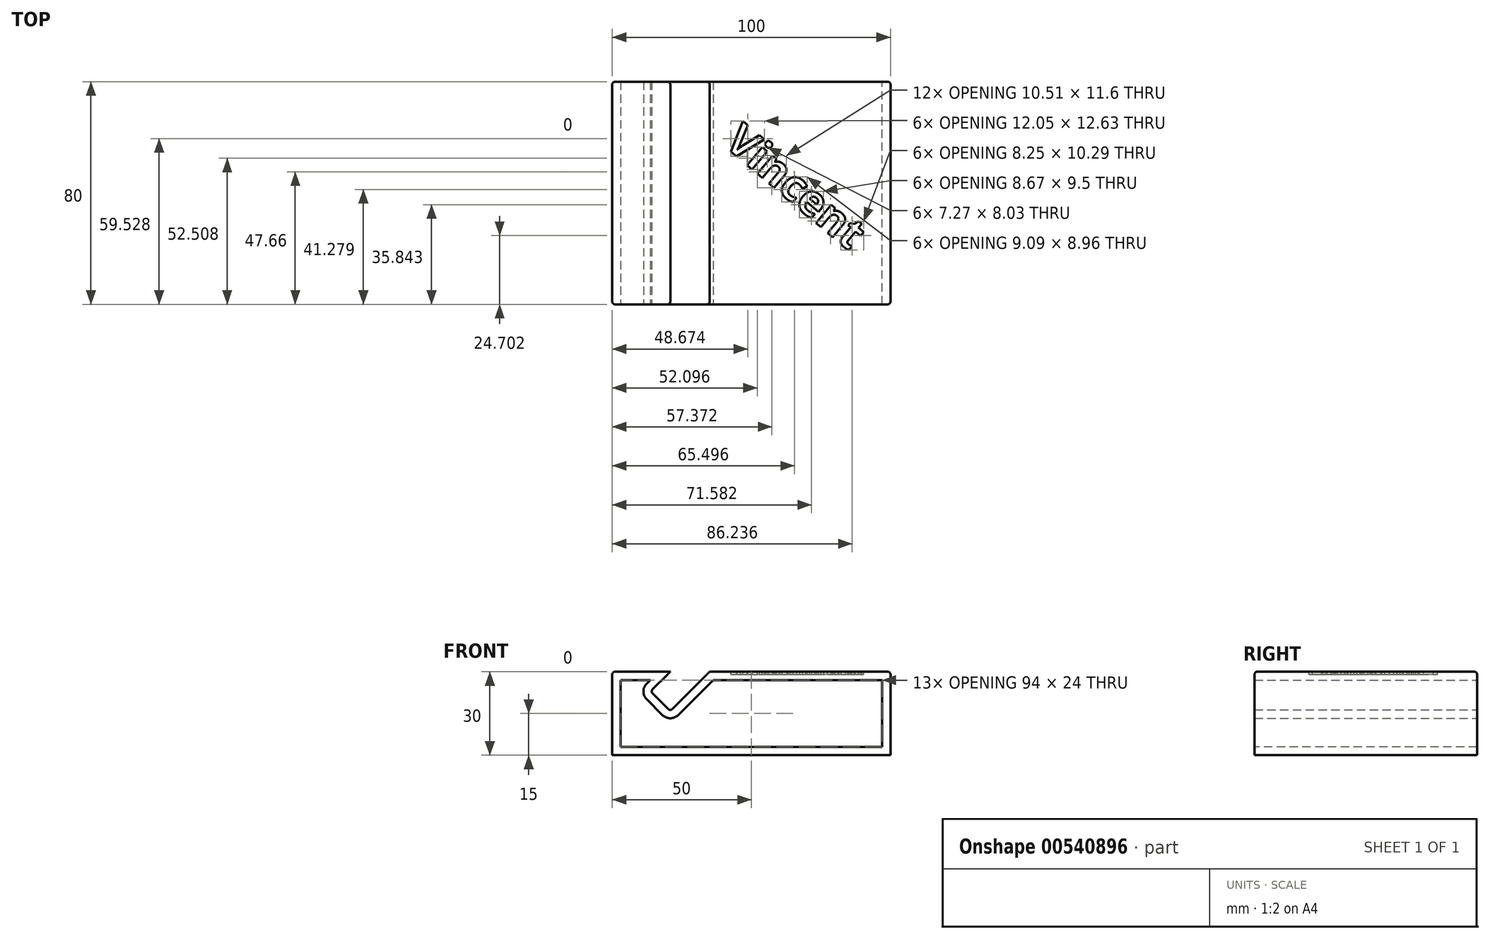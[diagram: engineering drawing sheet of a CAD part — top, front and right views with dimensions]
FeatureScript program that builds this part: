
annotation { "Feature Type Name" : "Feature", "Feature Type Description" : "" }
export const myFeature = defineFeature(function(context is Context, id is Id, definition is map)
    precondition{}
    {
        {
            var Q0;
            Q0=qCreatedBy(makeId("Top.planeOp"),FACE);
            var sketch = newSketch(context, id + "F0", { "sketchPlane" : qUnion([Q0])});
            skLineSegment(sketch, "E0.bottom", {"start": v(-45.15, 40.95) * mm, "end": v(54.85, 40.95) * mm});
            skLineSegment(sketch, "E0.top", {"start": v(-45.15, -39.05) * mm, "end": v(54.85, -39.05) * mm});
            skLineSegment(sketch, "E0.left", {"start": v(-45.15, 40.95) * mm, "end": v(-45.15, -39.05) * mm});
            skLineSegment(sketch, "E0.right", {"start": v(54.85, 40.95) * mm, "end": v(54.85, -39.05) * mm});
            skSolve(sketch);
        }
        {
            var Q0;
            Q0=makeQuery(id+"F0.imprint","IMPRINT",FACE,{"disambiguationData":[TD([[makeQuery(id+"F0.imprint","IMPRINT",EDGE,{"derivedFrom":sQuery(id+"F0.wireOp",EDGE,"E0.bottom")}),-1.0]])]});
            extrude(context, id + "F1", {"entities" : qUnion([Q0]), "depth" : 30 * mm, "offsetDistance" : 25 * mm});
        }
        {
            var Q0;
            Q0=makeQuery(id+"F1.opExtrude","SWEPT_FACE",FACE,{"disambiguationData":[OSD([sQuery(id+"F0.wireOp",EDGE,"E0.top")])]});
            var sketch = newSketch(context, id + "F2", { "sketchPlane" : qUnion([Q0])});
            skLineSegment(sketch, "E1.bottom", {"start": v(-10.15, 30) * mm, "end": v(-24.3, 15.86) * mm});
            skLineSegment(sketch, "E1.top", {"start": v(-17.22, 37.07) * mm, "end": v(-31.36, 22.93) * mm});
            skLineSegment(sketch, "E1.left", {"start": v(-10.15, 30) * mm, "end": v(-17.22, 37.07) * mm});
            skLineSegment(sketch, "E1.right", {"start": v(-24.3, 15.86) * mm, "end": v(-31.36, 22.93) * mm});
            skSolve(sketch);
        }
        {
            var Q0;
            {var subQ0=sQuery(id+"F2.wireOp",EDGE,"E1.bottom");Q0=makeQuery(id+"F2.imprint","IMPRINT",FACE,{"disambiguationData":[TD([[makeQuery(id+"F2.imprint","IMPRINT",EDGE,{"derivedFrom":subQ0}),-1.0]])]});}
            extrude(context, id + "F3", {"entities" : qUnion([Q0]), "operationType" : NewBodyOperationType.REMOVE, "oppositeDirection" : true, "depth" : 80 * mm, "offsetDistance" : 25 * mm});
        }
        {
            var Q0;
            Q0=makeQuery(id+"F3.boolean.opBoolean","COPY",EDGE,{"derivedFrom":makeQuery(id+"F3.opExtrude","SWEPT_EDGE",EDGE,{"disambiguationData":[OSD([sQuery(id+"F0.wireOp",EDGE,"E0.top"),sQuery(id+"F2.wireOp",EDGE,"E1.top")])]})});
            var Q1;
            Q1=makeQuery(id+"F1.opExtrude","CAP_EDGE",EDGE,{"disambiguationData":[OSD([sQuery(id+"F0.wireOp",EDGE,"E0.left")])],"isStart":false});
            var Q2;
            {var subQ0=sQuery(id+"F0.wireOp",EDGE,"E0.left");var subQ1=sQuery(id+"F0.wireOp",EDGE,"E0.top");Q2=makeQuery(id+"F3.boolean.opBoolean","SPLIT",EDGE,{"disambiguationData":[TD([makeQuery(id+"F1.opExtrude","SWEPT_FACE",FACE,{"disambiguationData":[OSD([subQ0])]})])],"derivedFrom":makeQuery(id+"F1.opExtrude","CAP_EDGE",EDGE,{"disambiguationData":[OSD([subQ1])],"isStart":false})});}
            var Q3;
            {var subQ0=sQuery(id+"F0.wireOp",EDGE,"E0.right");var subQ1=sQuery(id+"F0.wireOp",EDGE,"E0.top");Q3=makeQuery(id+"F3.boolean.opBoolean","SPLIT",EDGE,{"disambiguationData":[TD([makeQuery(id+"F1.opExtrude","SWEPT_FACE",FACE,{"disambiguationData":[OSD([subQ0])]})])],"derivedFrom":makeQuery(id+"F1.opExtrude","CAP_EDGE",EDGE,{"disambiguationData":[OSD([subQ1])],"isStart":false})});}
            var Q4;
            Q4=makeQuery(id+"F1.opExtrude","CAP_EDGE",EDGE,{"disambiguationData":[OSD([sQuery(id+"F0.wireOp",EDGE,"E0.right")])],"isStart":false});
            var Q5;
            {var subQ0=sQuery(id+"F0.wireOp",EDGE,"E0.bottom");var subQ1=sQuery(id+"F0.wireOp",EDGE,"E0.right");Q5=makeQuery(id+"F3.boolean.opBoolean","SPLIT",EDGE,{"disambiguationData":[TD([makeQuery(id+"F1.opExtrude","SWEPT_FACE",FACE,{"disambiguationData":[OSD([subQ1])]})])],"derivedFrom":makeQuery(id+"F1.opExtrude","CAP_EDGE",EDGE,{"disambiguationData":[OSD([subQ0])],"isStart":false})});}
            var Q6;
            {var subQ0=sQuery(id+"F0.wireOp",EDGE,"E0.bottom");var subQ1=sQuery(id+"F0.wireOp",EDGE,"E0.left");Q6=makeQuery(id+"F3.boolean.opBoolean","SPLIT",EDGE,{"disambiguationData":[TD([makeQuery(id+"F1.opExtrude","SWEPT_FACE",FACE,{"disambiguationData":[OSD([subQ1])]})])],"derivedFrom":makeQuery(id+"F1.opExtrude","CAP_EDGE",EDGE,{"disambiguationData":[OSD([subQ0])],"isStart":false})});}
            var Q7;
            Q7=makeQuery(id+"F1.opExtrude","SWEPT_EDGE",EDGE,{"disambiguationData":[OSD([sQuery(id+"F0.wireOp",EDGE,"E0.bottom"),sQuery(id+"F0.wireOp",EDGE,"E0.right")])]});
            var Q8;
            Q8=makeQuery(id+"F1.opExtrude","SWEPT_EDGE",EDGE,{"disambiguationData":[OSD([sQuery(id+"F0.wireOp",EDGE,"E0.bottom"),sQuery(id+"F0.wireOp",EDGE,"E0.left")])]});
            var Q9;
            Q9=makeQuery(id+"F1.opExtrude","SWEPT_EDGE",EDGE,{"disambiguationData":[OSD([sQuery(id+"F0.wireOp",EDGE,"E0.top"),sQuery(id+"F0.wireOp",EDGE,"E0.left")])]});
            var Q10;
            Q10=makeQuery(id+"F1.opExtrude","SWEPT_EDGE",EDGE,{"disambiguationData":[OSD([sQuery(id+"F0.wireOp",EDGE,"E0.top"),sQuery(id+"F0.wireOp",EDGE,"E0.right")])]});
            var Q11;
            Q11=makeQuery(id+"F3.boolean.opBoolean","COPY",EDGE,{"derivedFrom":makeQuery(id+"F3.opExtrude","SWEPT_EDGE",EDGE,{"disambiguationData":[OSD([sQuery(id+"F2.wireOp",EDGE,"E1.bottom"),sQuery(id+"F2.wireOp",EDGE,"E1.right")])]})});
            var Q12;
            Q12=makeQuery(id+"F3.boolean.opBoolean","COPY",EDGE,{"derivedFrom":makeQuery(id+"F3.opExtrude","SWEPT_EDGE",EDGE,{"disambiguationData":[OSD([sQuery(id+"F2.wireOp",EDGE,"E1.top"),sQuery(id+"F2.wireOp",EDGE,"E1.right")])]})});
            fillet(context, id + "F4", {"entities" : qUnion([Q0, Q1, Q2, Q3, Q4, Q5, Q6, Q7, Q8, Q9, Q10, Q11, Q12]), "radius" : 1 * mm, "tangentPropagation" : true, "allowEdgeOverflow" : false});
        }
        {
            var Q0;
            Q0=makeQuery(id+"F1.opExtrude","SWEPT_FACE",FACE,{"disambiguationData":[OSD([sQuery(id+"F0.wireOp",EDGE,"E0.top")])]});
            var Q1;
            Q1=makeQuery(id+"F1.opExtrude","SWEPT_FACE",FACE,{"disambiguationData":[OSD([sQuery(id+"F0.wireOp",EDGE,"E0.bottom")])]});
            shell(context, id + "F5", {"entities" : qUnion([Q0, Q1]), "thickness" : 3 * mm});
        }
        {
            var Q0;
            {var subQ0=sQuery(id+"F0.wireOp",EDGE,"E0.bottom");var subQ1=sQuery(id+"F0.wireOp",EDGE,"E0.right");var subQ2=sQuery(id+"F0.wireOp",EDGE,"E0.top");Q0=makeQuery(id+"F3.boolean.opBoolean","SPLIT",FACE,{"disambiguationData":[TD([makeQuery(id+"F1.opExtrude","SWEPT_FACE",FACE,{"disambiguationData":[OSD([subQ1])]})])],"derivedFrom":makeQuery(id+"F1.opExtrude","CAP_FACE",FACE,{"disambiguationData":[OSD([subQ0,subQ2,sQuery(id+"F0.wireOp",EDGE,"E0.left"),subQ1])],"isStart":false})});}
            var sketch = newSketch(context, id + "F6", { "sketchPlane" : qUnion([Q0])});
            skText(sketch, "E2", { "text": "Vincent", "fontName": "OpenSans-Bold.ttf"});
            const initialGuessF6  = {"E2": [-0.0054, 0.01825, 0.76604, -0.64279, 0.01125]};
            skSetInitialGuess(sketch, initialGuessF6);
            skSolve(sketch);
        }
        {
            var Q0;
            Q0 = qSketchRegion(id + "F6", true);
            extrude(context, id + "F7", {"entities" : qUnion([Q0]), "operationType" : NewBodyOperationType.REMOVE, "oppositeDirection" : true, "depth" : 1 * mm, "offsetDistance" : 25 * mm});
        }
    });
